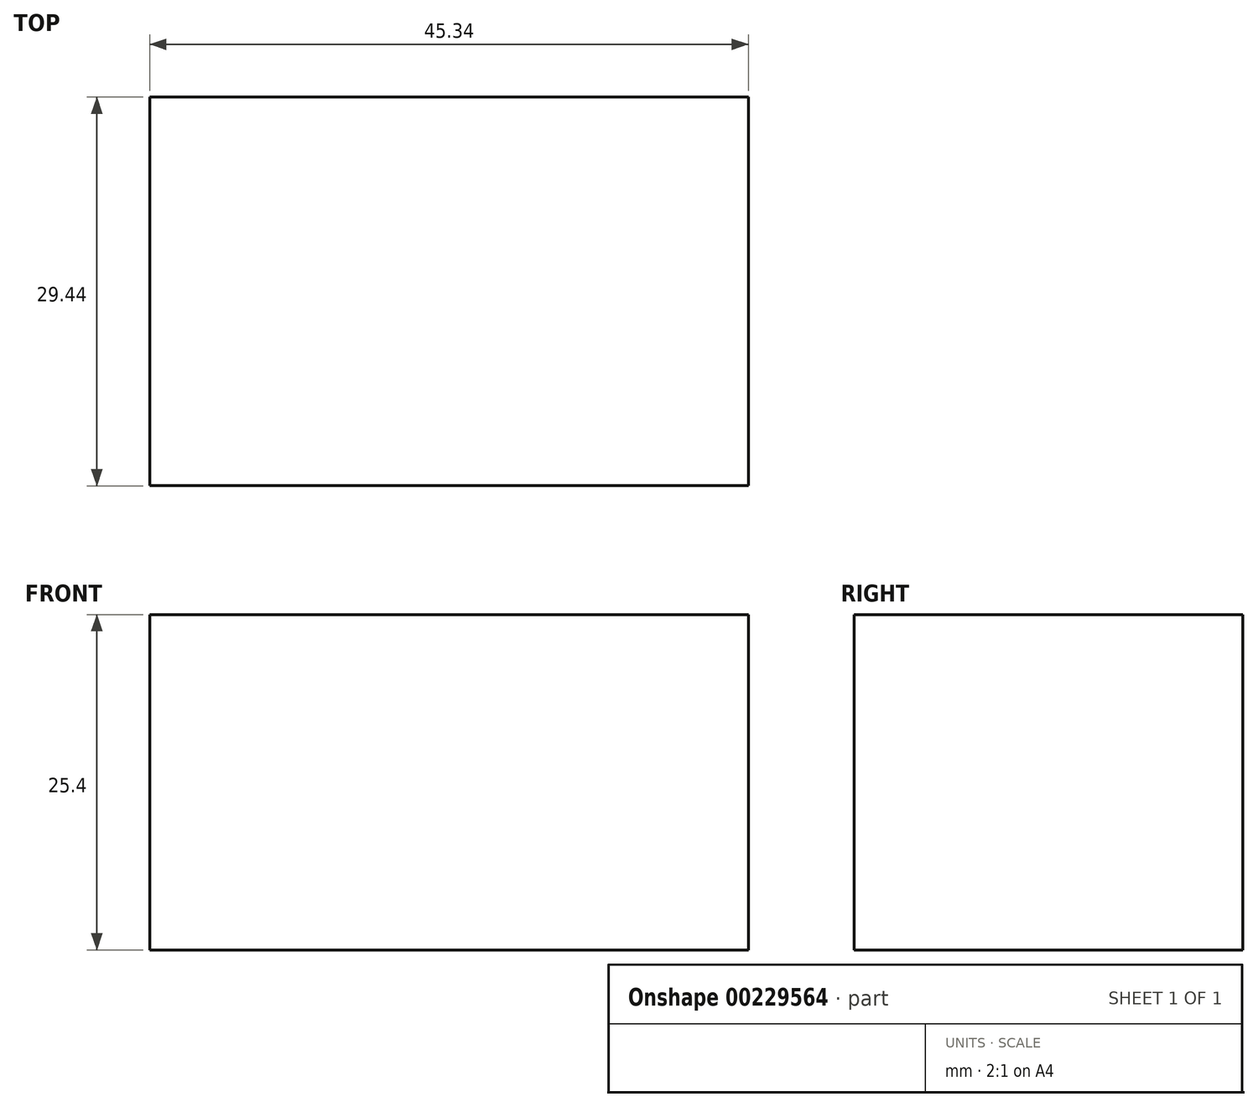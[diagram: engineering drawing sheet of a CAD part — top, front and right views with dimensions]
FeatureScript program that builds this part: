
annotation { "Feature Type Name" : "Feature", "Feature Type Description" : "" }
export const myFeature = defineFeature(function(context is Context, id is Id, definition is map)
    precondition{}
    {
        {
            var Q0;
            Q0=qCreatedBy(makeId("Top.planeOp"),FACE);
            var sketch = newSketch(context, id + "F0", { "sketchPlane" : qUnion([Q0])});
            skLineSegment(sketch, "E0.bottom", {"start": v(-22.67, 14.72) * mm, "end": v(22.67, 14.72) * mm});
            skLineSegment(sketch, "E0.top", {"start": v(-22.67, -14.72) * mm, "end": v(22.67, -14.72) * mm});
            skLineSegment(sketch, "E0.left", {"start": v(-22.67, 14.72) * mm, "end": v(-22.67, -14.72) * mm});
            skLineSegment(sketch, "E0.right", {"start": v(22.67, 14.72) * mm, "end": v(22.67, -14.72) * mm});
            skPoint(sketch, "E0.middle", {"position": v(0, 0) * mm});
            skSolve(sketch);
        }
        {
            var Q0;
            Q0=makeQuery(id+"F0.imprint","IMPRINT",FACE,{"disambiguationData":[TD([[makeQuery(id+"F0.imprint","IMPRINT",EDGE,{"derivedFrom":sQuery(id+"F0.wireOp",EDGE,"E0.bottom")}),-1.0]])]});
            extrude(context, id + "F1", {"entities" : qUnion([Q0]), "depth" : 25.4 * mm});
        }
    });
